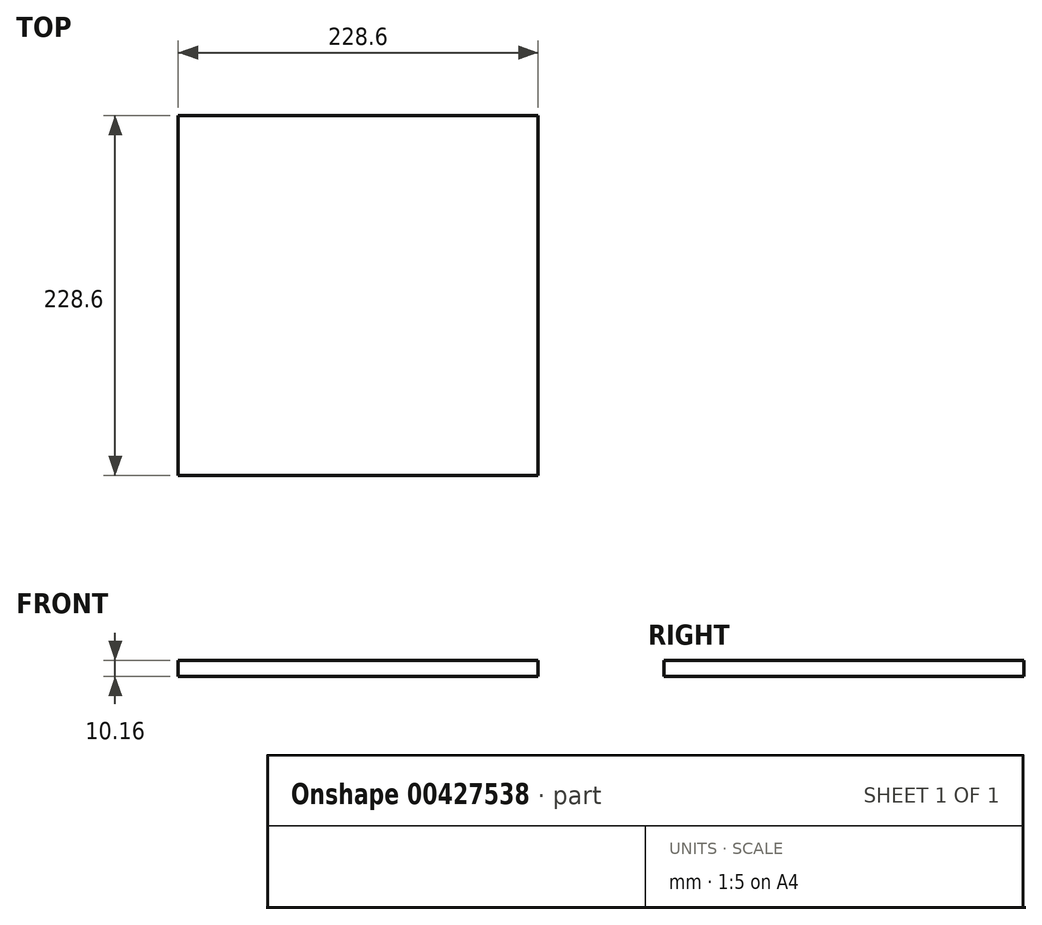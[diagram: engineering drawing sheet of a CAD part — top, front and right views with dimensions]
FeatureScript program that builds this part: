
annotation { "Feature Type Name" : "Feature", "Feature Type Description" : "" }
export const myFeature = defineFeature(function(context is Context, id is Id, definition is map)
    precondition{}
    {
        {
            var Q0;
            Q0=qCreatedBy(makeId("Top.planeOp"),FACE);
            var sketch = newSketch(context, id + "F0", { "sketchPlane" : qUnion([Q0])});
            skLineSegment(sketch, "E0.bottom", {"start": v(-115.76, 141.88) * mm, "end": v(112.84, 141.88) * mm});
            skLineSegment(sketch, "E0.top", {"start": v(-115.76, -86.72) * mm, "end": v(112.84, -86.72) * mm});
            skLineSegment(sketch, "E0.left", {"start": v(-115.76, 141.88) * mm, "end": v(-115.76, -86.72) * mm});
            skLineSegment(sketch, "E0.right", {"start": v(112.84, 141.88) * mm, "end": v(112.84, -86.72) * mm});
            skSolve(sketch);
        }
        {
            var Q0;
            Q0 = qSketchRegion(id + "F0", true);
            extrude(context, id + "F1", {"entities" : qUnion([Q0]), "depth" : 10.16 * mm});
        }
    });
